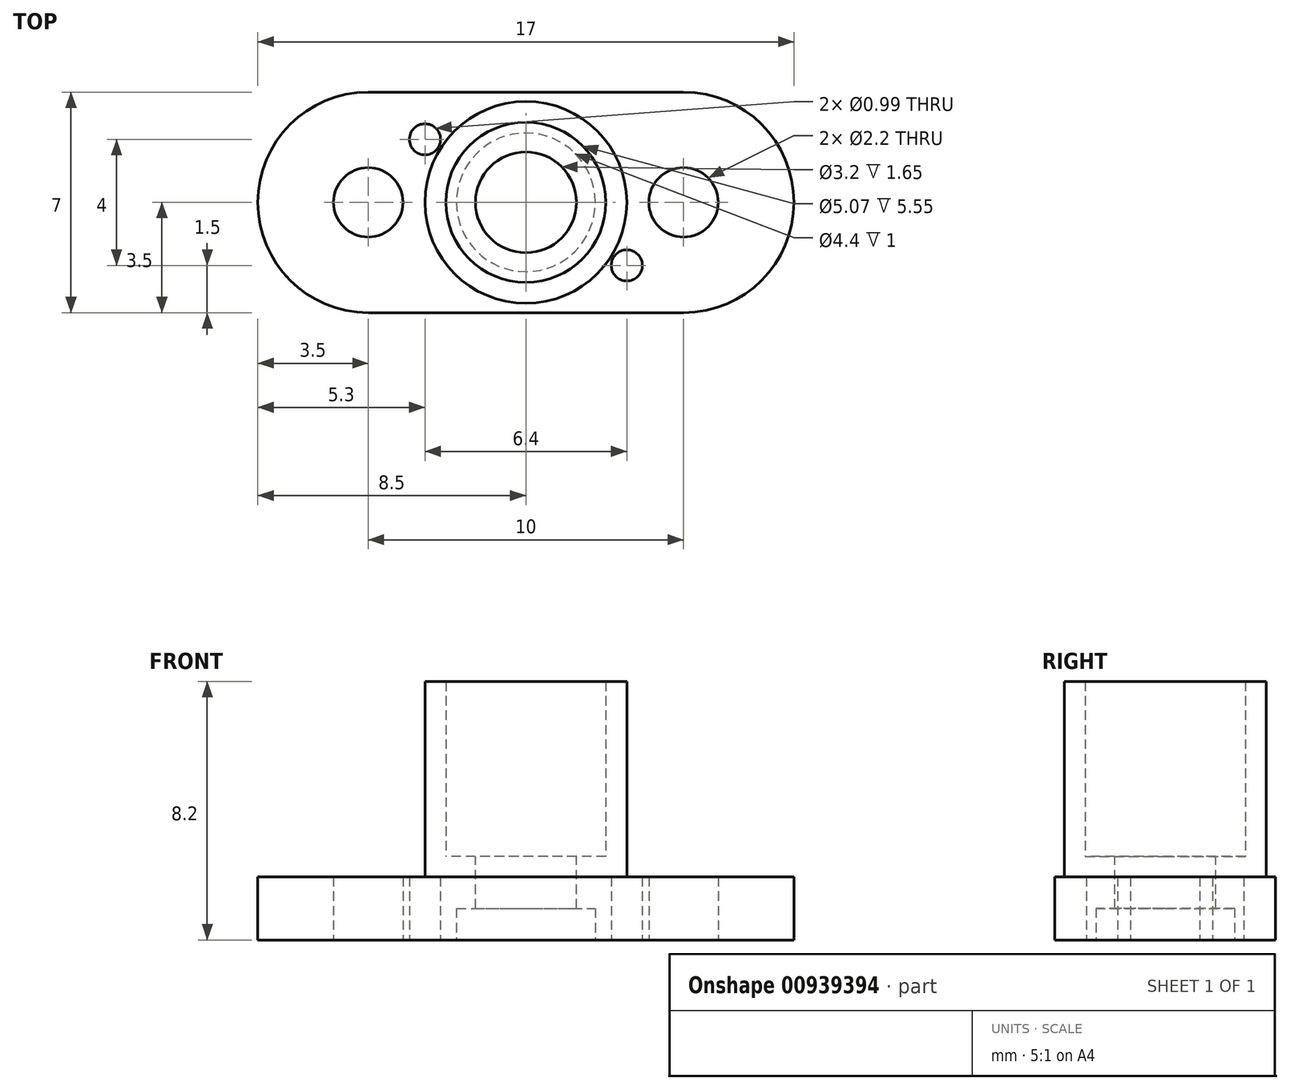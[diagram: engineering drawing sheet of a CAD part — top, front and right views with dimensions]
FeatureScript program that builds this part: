
annotation { "Feature Type Name" : "Feature", "Feature Type Description" : "" }
export const myFeature = defineFeature(function(context is Context, id is Id, definition is map)
    precondition{}
    {
        {
            var Q0;
            Q0=qCreatedBy(makeId("Top.planeOp"),FACE);
            var sketch = newSketch(context, id + "F0", { "sketchPlane" : qUnion([Q0])});
            skArc(sketch, "E0", {"start": v(-5, 3.5) * mm, "mid": v(-8.5, 0) * mm, "end": v(-5, -3.5) * mm});
            skArc(sketch, "E1", {"start": v(5, 3.5) * mm, "mid": v(8.5, 0) * mm, "end": v(5, -3.5) * mm});
            skLineSegment(sketch, "E2", {"start": v(-5, 3.5) * mm, "end": v(5, 3.5) * mm});
            skLineSegment(sketch, "E3", {"start": v(-5, -3.5) * mm, "end": v(5, -3.5) * mm});
            skCircle(sketch, "E4", {"center": v(-5, 0) * mm, "radius": 1.1 * mm});
            skCircle(sketch, "E5", {"center": v(5, 0) * mm, "radius": 1.1 * mm});
            skCircle(sketch, "E6", {"center": v(-3.2, 2) * mm, "radius": 0.5 * mm});
            skCircle(sketch, "E7", {"center": v(3.2, -2) * mm, "radius": 0.5 * mm});
            skSolve(sketch);
        }
        {
            var Q0;
            Q0 = qSketchRegion(id + "F0", true);
            extrude(context, id + "F1", {"entities" : qUnion([Q0]), "depth" : 2 * mm, "offsetDistance" : 25 * mm});
        }
        {
            var Q0;
            Q0=makeQuery(id+"F1.opExtrude","CAP_FACE",FACE,{"disambiguationData":[OSD([sQuery(id+"F0.wireOp",EDGE,"E0"),sQuery(id+"F0.wireOp",EDGE,"E1"),sQuery(id+"F0.wireOp",EDGE,"E2"),sQuery(id+"F0.wireOp",EDGE,"E3"),sQuery(id+"F0.wireOp",EDGE,"E4"),sQuery(id+"F0.wireOp",EDGE,"E5"),sQuery(id+"F0.wireOp",EDGE,"E6"),sQuery(id+"F0.wireOp",EDGE,"E7")])],"isStart":false});
            var sketch = newSketch(context, id + "F2", { "sketchPlane" : qUnion([Q0])});
            skCircle(sketch, "E8", {"center": v(0, 0) * mm, "radius": 3.2 * mm});
            skSolve(sketch);
        }
        {
            var Q0;
            Q0 = qSketchRegion(id + "F2", true);
            extrude(context, id + "F3", {"entities" : qUnion([Q0]), "operationType" : NewBodyOperationType.ADD, "depth" : 0.65 * mm, "offsetDistance" : 25 * mm});
        }
        {
            var Q0;
            Q0=makeQuery(id+"F3.opExtrude","CAP_FACE",FACE,{"disambiguationData":[OSD([sQuery(id+"F2.wireOp",EDGE,"E8")])],"isStart":false});
            var sketch = newSketch(context, id + "F4", { "sketchPlane" : qUnion([Q0])});
            skCircle(sketch, "E9", {"center": v(0, 0) * mm, "radius": 3.2 * mm});
            skCircle(sketch, "E10", {"center": v(0, 0) * mm, "radius": 2.54 * mm});
            skSolve(sketch);
        }
        {
            var Q0;
            Q0 = qSketchRegion(id + "F4", true);
            extrude(context, id + "F5", {"entities" : qUnion([Q0]), "operationType" : NewBodyOperationType.ADD, "depth" : 5.55 * mm, "offsetDistance" : 25 * mm});
        }
        {
            var Q0;
            Q0=makeQuery(id+"F3.opExtrude","CAP_FACE",FACE,{"disambiguationData":[OSD([sQuery(id+"F2.wireOp",EDGE,"E8")])],"isStart":false});
            var sketch = newSketch(context, id + "F6", { "sketchPlane" : qUnion([Q0])});
            skCircle(sketch, "E11", {"center": v(0, 0) * mm, "radius": 1.6 * mm});
            skSolve(sketch);
        }
        {
            var Q0;
            Q0 = qSketchRegion(id + "F6", true);
            extrude(context, id + "F7", {"entities" : qUnion([Q0]), "operationType" : NewBodyOperationType.REMOVE, "oppositeDirection" : true, "depth" : 25 * mm, "offsetDistance" : 25 * mm});
        }
        {
            var Q0;
            Q0=makeQuery(id+"F1.opExtrude","CAP_FACE",FACE,{"disambiguationData":[OSD([sQuery(id+"F0.wireOp",EDGE,"E0"),sQuery(id+"F0.wireOp",EDGE,"E1"),sQuery(id+"F0.wireOp",EDGE,"E2"),sQuery(id+"F0.wireOp",EDGE,"E3"),sQuery(id+"F0.wireOp",EDGE,"E4"),sQuery(id+"F0.wireOp",EDGE,"E5"),sQuery(id+"F0.wireOp",EDGE,"E6"),sQuery(id+"F0.wireOp",EDGE,"E7")])],"isStart":true});
            var sketch = newSketch(context, id + "F8", { "sketchPlane" : qUnion([Q0])});
            skCircle(sketch, "E12", {"center": v(0, 0) * mm, "radius": 2.2 * mm});
            skSolve(sketch);
        }
        {
            var Q0;
            Q0 = qSketchRegion(id + "F8", true);
            extrude(context, id + "F9", {"entities" : qUnion([Q0]), "operationType" : NewBodyOperationType.REMOVE, "oppositeDirection" : true, "depth" : 1 * mm, "offsetDistance" : 25 * mm});
        }
    });
